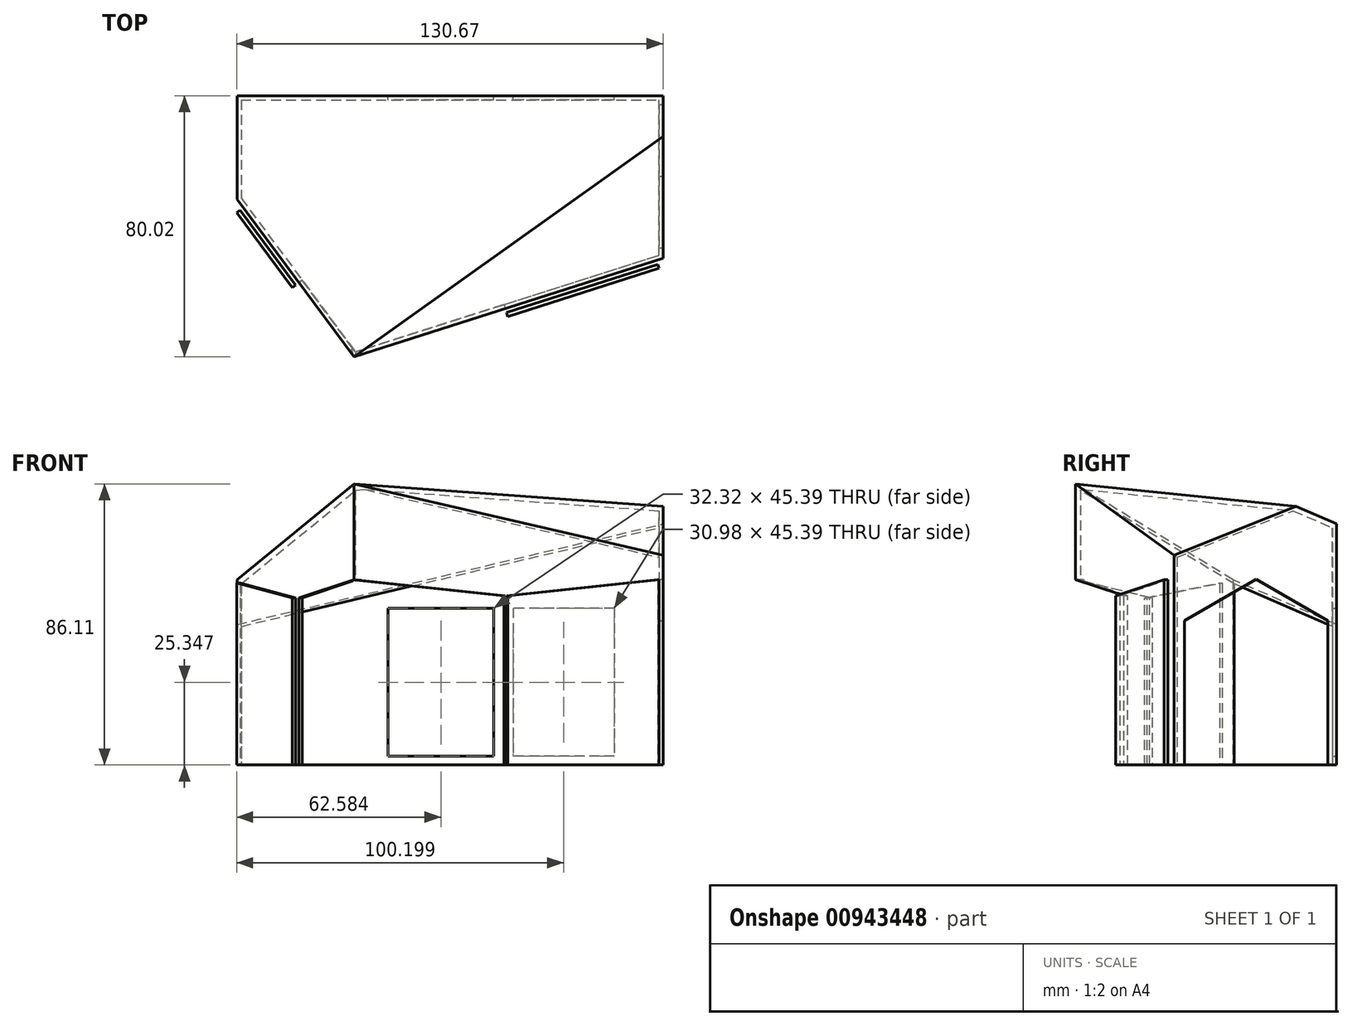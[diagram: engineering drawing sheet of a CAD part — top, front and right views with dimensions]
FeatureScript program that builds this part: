
annotation { "Feature Type Name" : "Feature", "Feature Type Description" : "" }
export const myFeature = defineFeature(function(context is Context, id is Id, definition is map)
    precondition{}
    {
        {
            var Q0;
            Q0=qCreatedBy(makeId("Top.planeOp"),FACE);
            var sketch = newSketch(context, id + "F0", { "sketchPlane" : qUnion([Q0])});
            skLineSegment(sketch, "E0", {"start": v(-66.67, 46.62) * mm, "end": v(63.88, 46.62) * mm});
            skLineSegment(sketch, "E1", {"start": v(-66.67, 46.62) * mm, "end": v(-66.67, 14.86) * mm});
            skLineSegment(sketch, "E2", {"start": v(-66.67, 14.86) * mm, "end": v(-30.86, -33.4) * mm});
            skLineSegment(sketch, "E3", {"start": v(-30.86, -33.4) * mm, "end": v(63.88, -3.18) * mm});
            skLineSegment(sketch, "E4", {"start": v(63.88, -3.18) * mm, "end": v(63.88, 46.62) * mm});
            skSolve(sketch);
        }
        {
            var Q0;
            Q0=makeQuery(id+"F0.imprint","IMPRINT",FACE,{"disambiguationData":[TD([[makeQuery(id+"F0.imprint","IMPRINT",EDGE,{"derivedFrom":sQuery(id+"F0.wireOp",EDGE,"E0")}),-1.0]])]});
            extrude(context, id + "F1", {"entities" : qUnion([Q0]), "depth" : 86.1 * mm, "offsetDistance" : 25.4 * mm});
        }
        {
            var Q0;
            Q0=makeQuery(id+"F1.opExtrude","CAP_FACE",FACE,{"disambiguationData":[OSD([sQuery(id+"F0.wireOp",EDGE,"E0"),sQuery(id+"F0.wireOp",EDGE,"E1"),sQuery(id+"F0.wireOp",EDGE,"E2"),sQuery(id+"F0.wireOp",EDGE,"E3"),sQuery(id+"F0.wireOp",EDGE,"E4")])],"isStart":false});
            var sketch = newSketch(context, id + "F2", { "sketchPlane" : qUnion([Q0])});
            skLineSegment(sketch, "E5", {"start": v(-30.86, -33.4) * mm, "end": v(13.92, 46.62) * mm});
            skSolve(sketch);
        }
        {
            var Q0;
            Q0=makeQuery(id+"F1.opExtrude","SWEPT_FACE",FACE,{"disambiguationData":[OSD([sQuery(id+"F0.wireOp",EDGE,"E0")])]});
            var sketch = newSketch(context, id + "F3", { "sketchPlane" : qUnion([Q0])});
            skLineSegment(sketch, "E6", {"start": v(-63.88, 43.05) * mm, "end": v(66.67, 43.05) * mm});
            skLineSegment(sketch, "E7", {"start": v(-63.88, 62.27) * mm, "end": v(66.67, 62.27) * mm});
            skLineSegment(sketch, "E8", {"start": v(-14.72, 62.27) * mm, "end": v(-14.72, 0.18) * mm});
            skSolve(sketch);
        }
        {
            var Q0;
            Q0=makeQuery(id+"F1.opExtrude","SWEPT_EDGE",EDGE,{"disambiguationData":[OSD([sQuery(id+"F0.wireOp",EDGE,"E0"),sQuery(id+"F0.wireOp",EDGE,"E1")])]});
            cPoint(context, id + "F4", {"entities" : qUnion([Q0]), "parameter" : 0.5});
        }
        {
            var Q0;
            Q0=sQuery(id+"F3.wireOp",VERTEX,"E8.start");
            var Q1;
            Q1=sQuery(id+"F2.wireOp",VERTEX,"E5.start");
            var Q2;
            Q2 = qCreatedBy(id + "F4" ,VERTEX);
            cPlane(context, id + "F5", {"entities" : qUnion([Q0, Q1, Q2]), "cplaneType" : CPlaneType.THREE_POINT, "offset" : 25.4 * mm, "width" : 152.4 * mm, "height" : 152.4 * mm});
        }
        {
            var Q0;
            Q0=qCreatedBy(id+"F5.planeOp",FACE);
            var sketch = newSketch(context, id + "F6", { "sketchPlane" : qUnion([Q0])});
            skLineSegment(sketch, "E9.bottom", {"start": v(112.7, -70.14) * mm, "end": v(-127.55, -70.14) * mm});
            skLineSegment(sketch, "E9.top", {"start": v(112.7, 77.8) * mm, "end": v(-127.55, 77.8) * mm});
            skLineSegment(sketch, "E9.left", {"start": v(112.7, -70.14) * mm, "end": v(112.7, 77.8) * mm});
            skLineSegment(sketch, "E9.right", {"start": v(-127.55, -70.14) * mm, "end": v(-127.55, 77.8) * mm});
            skSolve(sketch);
        }
        {
            var Q0;
            Q0=makeQuery(id+"F6.imprint","IMPRINT",FACE,{"disambiguationData":[TD([[makeQuery(id+"F6.imprint","IMPRINT",EDGE,{"derivedFrom":sQuery(id+"F6.wireOp",EDGE,"E9.bottom")}),-1.0]])]});
            var Q1;
            {var subQ0=sQuery(id+"F0.wireOp",EDGE,"E0");var subQ1=makeQuery(id+"F1.opExtrude","CAP_EDGE",EDGE,{"disambiguationData":[OSD([subQ0])],"isStart":false});Q1=makeQuery(id+"F3.imprint","IMPRINT",FACE,{"disambiguationData":[TD([[makeQuery(id+"F3.imprint","IMPRINT",EDGE,{"derivedFrom":subQ1}),1.0]])]});}
            extrude(context, id + "F7", {"entities" : qUnion([Q0, Q1]), "operationType" : NewBodyOperationType.REMOVE, "depth" : 60.7 * mm, "offsetDistance" : 25.4 * mm});
        }
        {
            var Q0;
            Q0=makeQuery(id+"F1.opExtrude","SWEPT_FACE",FACE,{"disambiguationData":[OSD([sQuery(id+"F0.wireOp",EDGE,"E4")])]});
            var sketch = newSketch(context, id + "F8", { "sketchPlane" : qUnion([Q0])});
            skLineSegment(sketch, "E10", {"start": v(34.16, 79.26) * mm, "end": v(-3.18, 79.26) * mm});
            skLineSegment(sketch, "E11", {"start": v(46.62, 64.3) * mm, "end": v(-3.18, 64.3) * mm});
            skSolve(sketch);
        }
        {
            var Q0;
            Q0=sQuery(id+"F2.wireOp",VERTEX,"E5.start");
            var Q1;
            Q1=sQuery(id+"F8.wireOp",VERTEX,"E10.start");
            var Q2;
            Q2=sQuery(id+"F8.wireOp",VERTEX,"E11.end");
            cPlane(context, id + "F9", {"entities" : qUnion([Q0, Q1, Q2]), "cplaneType" : CPlaneType.THREE_POINT, "offset" : 25.4 * mm, "width" : 152.4 * mm, "height" : 152.4 * mm});
        }
        {
            var Q0;
            Q0=qCreatedBy(id+"F9.planeOp",FACE);
            var sketch = newSketch(context, id + "F10", { "sketchPlane" : qUnion([Q0])});
            skLineSegment(sketch, "E12.bottom", {"start": v(72.31, -22.87) * mm, "end": v(-62.98, -22.87) * mm});
            skLineSegment(sketch, "E12.top", {"start": v(72.31, 71.76) * mm, "end": v(-62.98, 71.76) * mm});
            skLineSegment(sketch, "E12.left", {"start": v(72.31, -22.87) * mm, "end": v(72.31, 71.76) * mm});
            skLineSegment(sketch, "E12.right", {"start": v(-62.98, -22.87) * mm, "end": v(-62.98, 71.76) * mm});
            skSolve(sketch);
        }
        {
            var Q0;
            Q0=makeQuery(id+"F10.imprint","IMPRINT",FACE,{"disambiguationData":[TD([[makeQuery(id+"F10.imprint","IMPRINT",EDGE,{"derivedFrom":sQuery(id+"F10.wireOp",EDGE,"E12.bottom")}),-1.0]])]});
            extrude(context, id + "F11", {"entities" : qUnion([Q0]), "operationType" : NewBodyOperationType.REMOVE, "depth" : 41.15 * mm, "offsetDistance" : 25.4 * mm});
        }
        {
            var Q0;
            Q0=makeQuery(id+"F1.opExtrude","SWEPT_FACE",FACE,{"disambiguationData":[OSD([sQuery(id+"F0.wireOp",EDGE,"E2")])]});
            var sketch = newSketch(context, id + "F12", { "sketchPlane" : qUnion([Q0])});
            skLineSegment(sketch, "E13", {"start": v(-19.91, 0) * mm, "end": v(-19.91, 51.25) * mm});
            skLineSegment(sketch, "E14", {"start": v(-19.91, 51.25) * mm, "end": v(8.43, 56.79) * mm});
            skLineSegment(sketch, "E15", {"start": v(8.43, 56.79) * mm, "end": v(8.43, 0) * mm});
            skLineSegment(sketch, "E16", {"start": v(8.43, 0) * mm, "end": v(-19.91, 0) * mm});
            skLineSegment(sketch, "E17", {"start": v(-51.66, 56.79) * mm, "end": v(8.43, 56.79) * mm, "construction": true});
            skSolve(sketch);
        }
        {
            var Q0;
            Q0=makeQuery(id+"F1.opExtrude","CAP_FACE",FACE,{"disambiguationData":[OSD([sQuery(id+"F0.wireOp",EDGE,"E0"),sQuery(id+"F0.wireOp",EDGE,"E1"),sQuery(id+"F0.wireOp",EDGE,"E2"),sQuery(id+"F0.wireOp",EDGE,"E3"),sQuery(id+"F0.wireOp",EDGE,"E4")])],"isStart":true});
            shell(context, id + "F13", {"entities" : qUnion([Q0]), "thickness" : 1.27 * mm});
        }
        {
            var Q0;
            Q0=makeQuery(id+"F12.imprint","IMPRINT",FACE,{"disambiguationData":[TD([[makeQuery(id+"F12.imprint","IMPRINT",EDGE,{"derivedFrom":sQuery(id+"F12.wireOp",EDGE,"E13")}),-1.0]])]});
            extrude(context, id + "F14", {"entities" : qUnion([Q0]), "operationType" : NewBodyOperationType.REMOVE, "oppositeDirection" : true, "depth" : 2.54 * mm, "offsetDistance" : 25.4 * mm});
        }
        {
            var Q0;
            Q0=makeQuery(id+"F1.opExtrude","SWEPT_FACE",FACE,{"disambiguationData":[OSD([sQuery(id+"F0.wireOp",EDGE,"E3")])]});
            var sketch = newSketch(context, id + "F15", { "sketchPlane" : qUnion([Q0])});
            skLineSegment(sketch, "E18", {"start": v(-39.55, 56.79) * mm, "end": v(9.1, 51.88) * mm});
            skLineSegment(sketch, "E19", {"start": v(9.1, 51.88) * mm, "end": v(9.1, 0) * mm});
            skLineSegment(sketch, "E20", {"start": v(9.1, 0) * mm, "end": v(-39.55, 0) * mm});
            skLineSegment(sketch, "E21", {"start": v(-39.55, 0) * mm, "end": v(-39.55, 56.79) * mm});
            skSolve(sketch);
        }
        {
            var Q0;
            Q0=makeQuery(id+"F15.imprint","IMPRINT",FACE,{"disambiguationData":[TD([[makeQuery(id+"F15.imprint","IMPRINT",EDGE,{"derivedFrom":sQuery(id+"F15.wireOp",EDGE,"E18")}),-1.0]])]});
            extrude(context, id + "F16", {"entities" : qUnion([Q0]), "operationType" : NewBodyOperationType.REMOVE, "oppositeDirection" : true, "depth" : 2.54 * mm, "offsetDistance" : 25.4 * mm});
        }
        {
            var Q0;
            Q0=makeQuery(id+"F1.opExtrude","SWEPT_FACE",FACE,{"disambiguationData":[OSD([sQuery(id+"F0.wireOp",EDGE,"E4")])]});
            var sketch = newSketch(context, id + "F17", { "sketchPlane" : qUnion([Q0])});
            skLineSegment(sketch, "E22", {"start": v(0, 0) * mm, "end": v(0, 44.27) * mm});
            skLineSegment(sketch, "E23", {"start": v(0, 44.27) * mm, "end": v(22, 56.97) * mm});
            skLineSegment(sketch, "E24", {"start": v(22, 56.97) * mm, "end": v(44, 44.27) * mm});
            skLineSegment(sketch, "E25", {"start": v(44, 44.27) * mm, "end": v(44, 0) * mm});
            skLineSegment(sketch, "E26", {"start": v(44, 0) * mm, "end": v(0, 0) * mm});
            skSolve(sketch);
        }
        {
            var Q0;
            Q0=makeQuery(id+"F17.imprint","IMPRINT",FACE,{"disambiguationData":[TD([[makeQuery(id+"F17.imprint","IMPRINT",EDGE,{"derivedFrom":sQuery(id+"F17.wireOp",EDGE,"E22")}),-1.0]])]});
            extrude(context, id + "F18", {"entities" : qUnion([Q0]), "operationType" : NewBodyOperationType.REMOVE, "oppositeDirection" : true, "depth" : 2.54 * mm, "offsetDistance" : 25.4 * mm});
        }
        {
            var Q0;
            Q0=makeQuery(id+"F1.opExtrude","SWEPT_FACE",FACE,{"disambiguationData":[OSD([sQuery(id+"F0.wireOp",EDGE,"E0")])]});
            var sketch = newSketch(context, id + "F19", { "sketchPlane" : qUnion([Q0])});
            skLineSegment(sketch, "E27.bottom", {"start": v(-48.9, 48.04) * mm, "end": v(-17.92, 48.04) * mm});
            skLineSegment(sketch, "E27.top", {"start": v(-48.9, 2.65) * mm, "end": v(-17.92, 2.65) * mm});
            skLineSegment(sketch, "E27.left", {"start": v(-48.9, 48.04) * mm, "end": v(-48.9, 2.65) * mm});
            skLineSegment(sketch, "E27.right", {"start": v(-17.92, 48.04) * mm, "end": v(-17.92, 2.65) * mm});
            skLineSegment(sketch, "E28.bottom", {"start": v(-11.95, 48.04) * mm, "end": v(20.37, 48.04) * mm});
            skLineSegment(sketch, "E28.top", {"start": v(-11.95, 2.65) * mm, "end": v(20.37, 2.65) * mm});
            skLineSegment(sketch, "E28.left", {"start": v(-11.95, 48.04) * mm, "end": v(-11.95, 2.65) * mm});
            skLineSegment(sketch, "E28.right", {"start": v(20.37, 48.04) * mm, "end": v(20.37, 2.65) * mm});
            skSolve(sketch);
        }
        {
            var Q0;
            Q0=makeQuery(id+"F19.imprint","IMPRINT",FACE,{"disambiguationData":[TD([[makeQuery(id+"F19.imprint","IMPRINT",EDGE,{"derivedFrom":sQuery(id+"F19.wireOp",EDGE,"E27.bottom")}),-1.0]])]});
            var Q1;
            Q1=makeQuery(id+"F19.imprint","IMPRINT",FACE,{"disambiguationData":[TD([[makeQuery(id+"F19.imprint","IMPRINT",EDGE,{"derivedFrom":sQuery(id+"F19.wireOp",EDGE,"E28.bottom")}),-1.0]])]});
            extrude(context, id + "F20", {"entities" : qUnion([Q0, Q1]), "operationType" : NewBodyOperationType.REMOVE, "oppositeDirection" : true, "depth" : 2.54 * mm, "offsetDistance" : 25.4 * mm});
        }
        {
            var Q0;
            Q0 = qConstructionFilter(qBodyType(qCreatedBy(id + "F17" ,EDGE), BodyType.WIRE), ConstructionObject.NO);
            extrude(context, id + "F21", {"bodyType" : ToolBodyType.SURFACE, "surfaceEntities" : qUnion([Q0]), "depth" : 89.15 * mm, "offsetDistance" : 25.4 * mm});
        }
        {
            var Q0;
            Q0=makeQuery(id+"F1.opExtrude","SWEPT_FACE",FACE,{"disambiguationData":[OSD([sQuery(id+"F0.wireOp",EDGE,"E3")])]});
            var sketch = newSketch(context, id + "F22", { "sketchPlane" : qUnion([Q0])});
            skLineSegment(sketch, "E29", {"start": v(9.1, 51.88) * mm, "end": v(57.74, 56.78) * mm});
            skLineSegment(sketch, "E30", {"start": v(57.74, 0) * mm, "end": v(9.1, 0) * mm});
            skLineSegment(sketch, "E31", {"start": v(9.1, 0) * mm, "end": v(9.1, 51.88) * mm});
            skLineSegment(sketch, "E32", {"start": v(57.74, 56.78) * mm, "end": v(57.74, 0) * mm});
            skLineSegment(sketch, "E33", {"start": v(-39.55, 56.79) * mm, "end": v(59.9, 56.79) * mm, "construction": true});
            skSolve(sketch);
        }
        {
            var Q0;
            Q0=makeQuery(id+"F22.imprint","IMPRINT",FACE,{"disambiguationData":[TD([[makeQuery(id+"F22.imprint","IMPRINT",EDGE,{"derivedFrom":sQuery(id+"F22.wireOp",EDGE,"E29")}),-1.0]])]});
            extrude(context, id + "F23", {"entities" : qUnion([Q0]), "operationType" : NewBodyOperationType.ADD, "depth" : 2.54 * mm, "offsetDistance" : 25.4 * mm, "hasSecondDirection" : true, "secondDirectionOppositeDirection" : false, "secondDirectionDepth" : 1.27 * mm});
        }
        {
            var Q0;
            Q0=makeQuery(id+"F1.opExtrude","SWEPT_FACE",FACE,{"disambiguationData":[OSD([sQuery(id+"F0.wireOp",EDGE,"E2")])]});
            var sketch = newSketch(context, id + "F24", { "sketchPlane" : qUnion([Q0])});
            skLineSegment(sketch, "E34", {"start": v(-19.91, 51.25) * mm, "end": v(-48.44, 55.78) * mm});
            skLineSegment(sketch, "E35", {"start": v(-48.44, 55.78) * mm, "end": v(-48.44, 0) * mm});
            skLineSegment(sketch, "E36", {"start": v(-48.44, 0) * mm, "end": v(-19.91, 0) * mm});
            skLineSegment(sketch, "E37", {"start": v(-19.91, 0) * mm, "end": v(-19.91, 51.25) * mm});
            skLineSegment(sketch, "E38", {"start": v(-48.44, 55.78) * mm, "end": v(8.43, 56.79) * mm, "construction": true});
            skSolve(sketch);
        }
        {
            var Q0;
            Q0=makeQuery(id+"F24.imprint","IMPRINT",FACE,{"disambiguationData":[TD([[makeQuery(id+"F24.imprint","IMPRINT",EDGE,{"derivedFrom":sQuery(id+"F24.wireOp",EDGE,"E34")}),1.0]])]});
            extrude(context, id + "F25", {"entities" : qUnion([Q0]), "operationType" : NewBodyOperationType.ADD, "depth" : 2.54 * mm, "offsetDistance" : 25.4 * mm, "hasSecondDirection" : true, "secondDirectionOppositeDirection" : false, "secondDirectionDepth" : 1.27 * mm});
        }
    });
